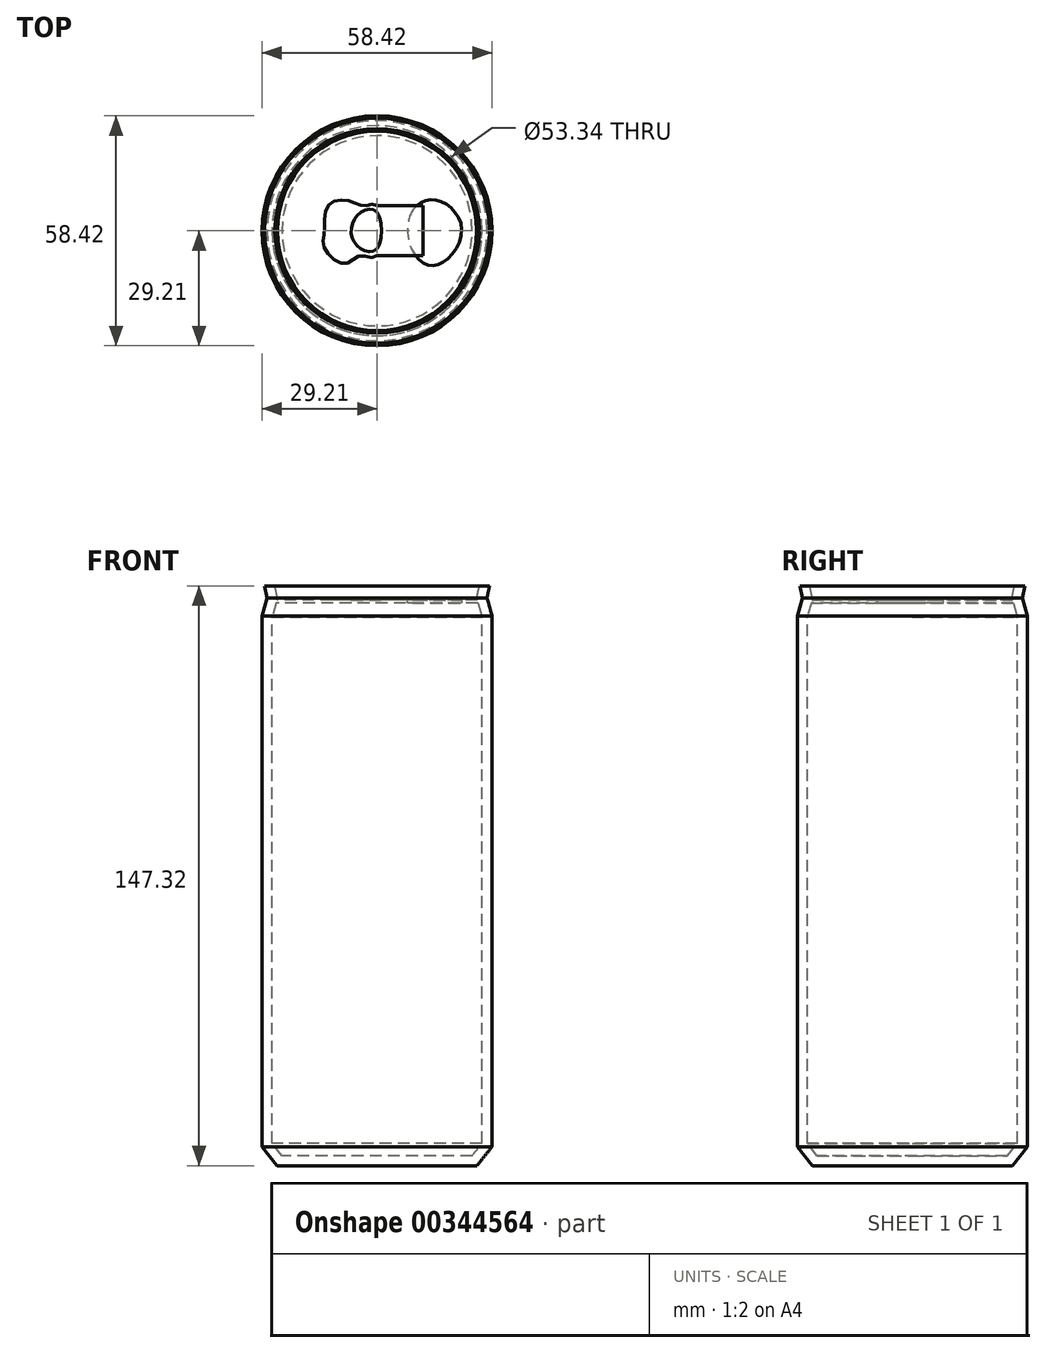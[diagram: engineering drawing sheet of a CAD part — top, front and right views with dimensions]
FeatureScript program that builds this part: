
annotation { "Feature Type Name" : "Feature", "Feature Type Description" : "" }
export const myFeature = defineFeature(function(context is Context, id is Id, definition is map)
    precondition{}
    {
        {
            var Q0;
            Q0=qCreatedBy(makeId("Top.planeOp"),FACE);
            var sketch = newSketch(context, id + "F0", { "sketchPlane" : qUnion([Q0])});
            skCircle(sketch, "E0", {"center": v(0, 0) * mm, "radius": 25.4 * mm});
            skSolve(sketch);
        }
        {
            var Q0;
            Q0=qCreatedBy(makeId("Top.planeOp"),FACE);
            cPlane(context, id + "F1", {"entities" : qUnion([Q0]), "cplaneType" : CPlaneType.OFFSET, "offset" : 4.83 * mm, "width" : 152.4 * mm, "height" : 152.4 * mm});
        }
        {
            var Q0;
            Q0=qCreatedBy(id+"F1.planeOp",FACE);
            var sketch = newSketch(context, id + "F2", { "sketchPlane" : qUnion([Q0])});
            skCircle(sketch, "E1", {"center": v(0, 0) * mm, "radius": 29.21 * mm});
            skSolve(sketch);
        }
        {
            var Q0;
            Q0=qCreatedBy(id+"F1.planeOp",FACE);
            cPlane(context, id + "F3", {"entities" : qUnion([Q0]), "cplaneType" : CPlaneType.OFFSET, "offset" : 134.87 * mm, "width" : 152.4 * mm, "height" : 152.4 * mm});
        }
        {
            var Q0;
            Q0=qCreatedBy(id+"F3.planeOp",FACE);
            var sketch = newSketch(context, id + "F4", { "sketchPlane" : qUnion([Q0])});
            skCircle(sketch, "E2", {"center": v(0, 0) * mm, "radius": 29.2 * mm});
            skSolve(sketch);
        }
        {
            var Q0;
            Q0 = qSketchRegion(id + "F2", true);
            var Q1;
            Q1 = qSketchRegion(id + "F4", true);
            loft(context, id + "F5", {"sheetProfilesArray" : [{ "sheetProfileEntities" : qUnion([Q0]) }, { "sheetProfileEntities" : qUnion([Q1]) }]});
        }
        {
            var Q1;
            Q1 = qSketchRegion(id + "F0", true);
            var Q2;
            Q2 = qSketchRegion(id + "F2", true);
            loft(context, id + "F6", {"operationType" : NewBodyOperationType.ADD, "sheetProfilesArray" : [{ "sheetProfileEntities" : qUnion([Q1]) }, { "sheetProfileEntities" : qUnion([Q2]) }]});
        }
        {
            var Q0;
            Q0=qCreatedBy(id+"F3.planeOp",FACE);
            cPlane(context, id + "F7", {"entities" : qUnion([Q0]), "cplaneType" : CPlaneType.OFFSET, "offset" : 4.57 * mm, "width" : 152.4 * mm, "height" : 152.4 * mm});
        }
        {
            var Q0;
            Q0=qCreatedBy(id+"F7.planeOp",FACE);
            var sketch = newSketch(context, id + "F8", { "sketchPlane" : qUnion([Q0])});
            skCircle(sketch, "E3", {"center": v(0, 0) * mm, "radius": 27.94 * mm});
            skSolve(sketch);
        }
        {
            var Q1;
            Q1 = qSketchRegion(id + "F4", true);
            var Q2;
            Q2 = qSketchRegion(id + "F8", true);
            loft(context, id + "F9", {"operationType" : NewBodyOperationType.ADD, "sheetProfilesArray" : [{ "sheetProfileEntities" : qUnion([Q1]) }, { "sheetProfileEntities" : qUnion([Q2]) }]});
        }
        {
            var Q0;
            Q0=qCreatedBy(id+"F7.planeOp",FACE);
            cPlane(context, id + "F10", {"entities" : qUnion([Q0]), "cplaneType" : CPlaneType.OFFSET, "offset" : 3.05 * mm, "width" : 152.4 * mm, "height" : 152.4 * mm});
        }
        {
            var Q0;
            Q0=qCreatedBy(id+"F10.planeOp",FACE);
            var sketch = newSketch(context, id + "F11", { "sketchPlane" : qUnion([Q0])});
            skCircle(sketch, "E4", {"center": v(0, 0) * mm, "radius": 28.58 * mm});
            skSolve(sketch);
        }
        {
            var Q1;
            Q1 = qSketchRegion(id + "F8", true);
            var Q2;
            Q2 = qSketchRegion(id + "F11", true);
            loft(context, id + "F12", {"operationType" : NewBodyOperationType.ADD, "sheetProfilesArray" : [{ "sheetProfileEntities" : qUnion([Q1]) }, { "sheetProfileEntities" : qUnion([Q2]) }]});
        }
        {
            var Q0;
            Q0=makeQuery(id+"F12.opLoft","CAP_FACE",FACE,{"disambiguationData":[OSD([makeQuery(id+"F11.imprint","IMPRINT",FACE,{"disambiguationData":[TD([[makeQuery(id+"F11.imprint","IMPRINT",EDGE,{"derivedFrom":sQuery(id+"F11.wireOp",EDGE,"E4")}),1.0]])]})])],"isStart":true});
            shell(context, id + "F13", {"entities" : qUnion([Q0]), "thickness" : 2.54 * mm});
        }
        {
            var Q0;
            Q0=qCreatedBy(id+"F7.planeOp",FACE);
            var Q1;
            Q1 = qBodyType(qCreatedBy(id + "F15" ,EDGE), BodyType.WIRE);
            cPlane(context, id + "F14", {"entities" : qUnion([Q0, Q1]), "cplaneType" : CPlaneType.OFFSET, "offset" : 0.5 * mm, "oppositeDirection" : true, "width" : 152.4 * mm, "height" : 152.4 * mm});
        }
        {
            var Q0;
            Q0=qCreatedBy(id+"F14.planeOp",FACE);
            var sketch = newSketch(context, id + "F15", { "sketchPlane" : qUnion([Q0])});
            skCircle(sketch, "E5", {"center": v(0, 0) * mm, "radius": 27.94 * mm});
            skLineSegment(sketch, "E6", {"start": v(8.98, -5.08) * mm, "end": v(8.98, 0) * mm});
            skLineSegment(sketch, "E7", {"start": v(8.98, 0) * mm, "end": v(8.98, 5.08) * mm});
            skFitSpline(sketch, "E8", {"points": [v(8.98, -5.08) * mm, v(15.17, -8.69) * mm, v(21.52, 0) * mm, v(15.68, 7.63) * mm, v(8.98, 5.08) * mm, v(8.98, -5.08) * mm]});
            skSolve(sketch);
        }
        {
            var Q0;
            Q0 = qSketchRegion(id + "F15", true);
            extrude(context, id + "F16", {"entities" : qUnion([Q0]), "operationType" : NewBodyOperationType.ADD, "oppositeDirection" : true, "depth" : 0.76 * mm});
        }
        {
            var Q0;
            Q0=qCreatedBy(id+"F14.planeOp",FACE);
            var sketch = newSketch(context, id + "F17", { "sketchPlane" : qUnion([Q0])});
            skLineSegment(sketch, "E9", {"start": v(11.69, 0) * mm, "end": v(11.69, 6.35) * mm});
            skLineSegment(sketch, "E10", {"start": v(11.69, 0) * mm, "end": v(11.69, -6.35) * mm});
            skLineSegment(sketch, "E11", {"start": v(11.69, -6.35) * mm, "end": v(0, -6.35) * mm});
            skLineSegment(sketch, "E12", {"start": v(11.69, 6.35) * mm, "end": v(0, 6.35) * mm});
            skFitSpline(sketch, "E13", {"points": [v(0, 6.35) * mm, v(-3.2, 6.35) * mm, v(-7.5, 7.7) * mm, v(-12.5, 6.35) * mm, v(-13.43, 0) * mm, v(-13.32, -4.51) * mm, v(-8.32, -8.35) * mm, v(-4.13, -6.37) * mm, v(0, -6.35) * mm, v(0, 6.35) * mm]});
            skFitSpline(sketch, "E14", {"points": [v(0, 4.67) * mm, v(-4.13, 4.67) * mm, v(-6.57, 0) * mm, v(-4.25, -4.51) * mm, v(0, -4.51) * mm, v(0, 4.67) * mm]});
            skSolve(sketch);
        }
        {
            var Q0;
            Q0 = qSketchRegion(id + "F17", true);
            extrude(context, id + "F18", {"entities" : qUnion([Q0]), "operationType" : NewBodyOperationType.ADD, "depth" : 0.64 * mm});
        }
    });
